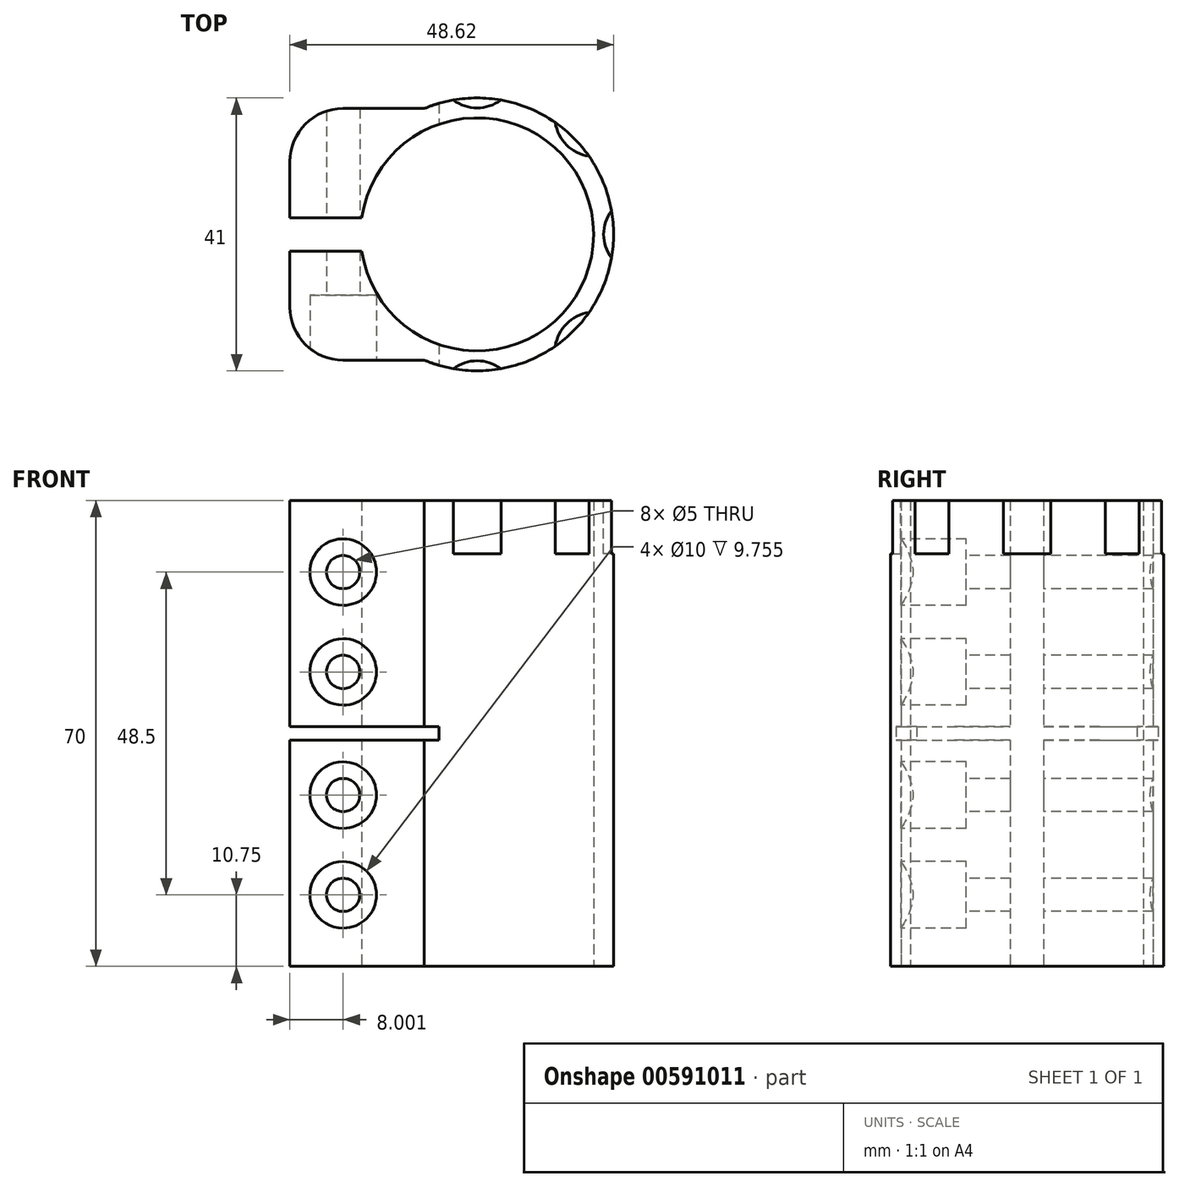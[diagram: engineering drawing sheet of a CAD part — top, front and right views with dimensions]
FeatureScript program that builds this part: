
annotation { "Feature Type Name" : "Feature", "Feature Type Description" : "" }
export const myFeature = defineFeature(function(context is Context, id is Id, definition is map)
    precondition{}
    {
        {
            var Q0;
            Q0=qCreatedBy(makeId("Top.planeOp"),FACE);
            var sketch = newSketch(context, id + "F0", { "sketchPlane" : qUnion([Q0])});
            skArc(sketch, "E0", {"start": v(-17.32, -2.5) * mm, "mid": v(17.5, 0) * mm, "end": v(-17.32, 2.5) * mm});
            skLineSegment(sketch, "E1", {"start": v(-7.92, 18.9) * mm, "end": v(-20.12, 18.9) * mm});
            skLineSegment(sketch, "E2", {"start": v(-28.12, 10.9) * mm, "end": v(-28.12, 2.5) * mm});
            skLineSegment(sketch, "E3", {"start": v(-28.12, 2.5) * mm, "end": v(-17.32, 2.5) * mm});
            skPoint(sketch, "E4.visualSharp", {"position": v(-28.12, 18.9) * mm});
            skArc(sketch, "E4.filletArc", {"start": v(-20.12, 18.9) * mm, "mid": v(-25.78, 16.57) * mm, "end": v(-28.12, 10.9) * mm});
            skLineSegment(sketch, "E5", {"start": v(0, 0) * mm, "end": v(62.93, 0) * mm, "construction": true});
            skLineSegment(sketch, "E6.MirrorCS", {"start": v(-28.12, -2.5) * mm, "end": v(-17.32, -2.5) * mm});
            skLineSegment(sketch, "E7.MirrorCS", {"start": v(-28.12, -10.9) * mm, "end": v(-28.12, -2.5) * mm});
            skArc(sketch, "E8.MirrorCS", {"start": v(-20.12, -18.9) * mm, "mid": v(-25.78, -16.57) * mm, "end": v(-28.12, -10.9) * mm});
            skLineSegment(sketch, "E9.MirrorCS", {"start": v(-7.92, -18.9) * mm, "end": v(-20.12, -18.9) * mm});
            skArc(sketch, "E10.trimOffspring", {"start": v(-7.92, -18.9) * mm, "mid": v(20.5, 0) * mm, "end": v(-7.92, 18.9) * mm});
            skSolve(sketch);
        }
        {
            var Q0;
            Q0 = qSketchRegion(id + "F0", true);
            extrude(context, id + "F1", {"entities" : qUnion([Q0]), "endBound" : BoundingType.SYMMETRIC, "depth" : 70 * mm, "offsetDistance" : 25 * mm});
        }
        {
            var Q0;
            Q0=makeQuery(id+"F1.opExtrude","SWEPT_FACE",FACE,{"disambiguationData":[OSD([sQuery(id+"F0.wireOp",EDGE,"E9.MirrorCS")])]});
            var sketch = newSketch(context, id + "F2", { "sketchPlane" : qUnion([Q0])});
            skPoint(sketch, "E11", {"position": v(-20.12, -24.25) * mm});
            skPoint(sketch, "E12", {"position": v(-20.12, -9.25) * mm});
            skPoint(sketch, "E13", {"position": v(-20.12, 9.25) * mm});
            skPoint(sketch, "E14", {"position": v(-20.12, 24.25) * mm});
            skSolve(sketch);
        }
        {
            var Q0;
            Q0=sQuery(id+"F2.wireOp",VERTEX,"E11");
            var Q1;
            Q1=sQuery(id+"F2.wireOp",VERTEX,"E12");
            var Q2;
            Q2=sQuery(id+"F2.wireOp",VERTEX,"E13");
            var Q3;
            Q3=sQuery(id+"F2.wireOp",VERTEX,"E14");
            var Q4;
            Q4=makeQuery(id+"F1.opExtrude","SWEPT_BODY",BODY,{"disambiguationData":[OSD([sQuery(id+"F0.wireOp",EDGE,"E0"),sQuery(id+"F0.wireOp",EDGE,"E1"),sQuery(id+"F0.wireOp",EDGE,"E2"),sQuery(id+"F0.wireOp",EDGE,"E3"),sQuery(id+"F0.wireOp",EDGE,"E4.filletArc"),sQuery(id+"F0.wireOp",EDGE,"E6.MirrorCS"),sQuery(id+"F0.wireOp",EDGE,"E7.MirrorCS"),sQuery(id+"F0.wireOp",EDGE,"E8.MirrorCS"),sQuery(id+"F0.wireOp",EDGE,"E9.MirrorCS"),sQuery(id+"F0.wireOp",EDGE,"E10.trimOffspring")])]});
            hole(context, id + "F3", {"style" : HoleStyle.C_BORE, "endStyle" : HoleEndStyle.THROUGH, "holeDiameter" : 5 * mm, "cBoreDiameter" : 10 * mm, "cBoreDepth" : 8 * mm, "majorDiameter" : 5 * mm, "isTappedThrough" : true, "tappedDepth" : 12 * mm, "tapClearance" : 3, "locations" : qUnion([Q0, Q1, Q2, Q3]), "scope" : qUnion([Q4])});
        }
        {
            var Q0;
            Q0=qCreatedBy(makeId("Front.planeOp"),FACE);
            var sketch = newSketch(context, id + "F4", { "sketchPlane" : qUnion([Q0])});
            skLineSegment(sketch, "E15.bottom", {"start": v(-28.12, 1) * mm, "end": v(-5.72, 1) * mm});
            skLineSegment(sketch, "E15.top", {"start": v(-28.12, -1) * mm, "end": v(-5.72, -1) * mm});
            skLineSegment(sketch, "E15.left", {"start": v(-28.12, 1) * mm, "end": v(-28.12, -1) * mm});
            skLineSegment(sketch, "E15.right", {"start": v(-5.72, 1) * mm, "end": v(-5.72, -1) * mm});
            skSolve(sketch);
        }
        {
            var Q0;
            Q0 = qSketchRegion(id + "F4", true);
            extrude(context, id + "F5", {"entities" : qUnion([Q0]), "operationType" : NewBodyOperationType.REMOVE, "endBound" : BoundingType.SYMMETRIC, "oppositeDirection" : true, "depth" : 50 * mm, "offsetDistance" : 25 * mm});
        }
        {
            var Q0;
            Q0=makeQuery(id+"F1.opExtrude","CAP_FACE",FACE,{"disambiguationData":[OSD([sQuery(id+"F0.wireOp",EDGE,"E0"),sQuery(id+"F0.wireOp",EDGE,"E1"),sQuery(id+"F0.wireOp",EDGE,"E2"),sQuery(id+"F0.wireOp",EDGE,"E3"),sQuery(id+"F0.wireOp",EDGE,"E4.filletArc"),sQuery(id+"F0.wireOp",EDGE,"E6.MirrorCS"),sQuery(id+"F0.wireOp",EDGE,"E7.MirrorCS"),sQuery(id+"F0.wireOp",EDGE,"E8.MirrorCS"),sQuery(id+"F0.wireOp",EDGE,"E9.MirrorCS"),sQuery(id+"F0.wireOp",EDGE,"E10.trimOffspring")])],"isStart":false});
            var sketch = newSketch(context, id + "F6", { "sketchPlane" : qUnion([Q0])});
            skCircle(sketch, "E16", {"center": v(0, -25) * mm, "radius": 6 * mm});
            skCircle(sketch, "E17.1.0", {"center": v(17.68, -17.68) * mm, "radius": 6 * mm});
            skCircle(sketch, "E17.2.0", {"center": v(25, 0) * mm, "radius": 6 * mm});
            skCircle(sketch, "E17.3.0", {"center": v(17.68, 17.68) * mm, "radius": 6 * mm});
            skCircle(sketch, "E17.4.0", {"center": v(0, 25) * mm, "radius": 6 * mm});
            skPoint(sketch, "E17.center", {"position": v(0, 0) * mm});
            skLineSegment(sketch, "E17.anchor1", {"start": v(0, 0) * mm, "end": v(0, -25) * mm, "construction": true});
            skLineSegment(sketch, "E17.anchor2", {"start": v(0, 0) * mm, "end": v(0, 25) * mm, "construction": true});
            skSolve(sketch);
        }
        {
            var Q0;
            Q0 = qSketchRegion(id + "F6", true);
            extrude(context, id + "F7", {"entities" : qUnion([Q0]), "operationType" : NewBodyOperationType.REMOVE, "oppositeDirection" : true, "depth" : 8 * mm, "offsetDistance" : 25 * mm});
        }
    });
